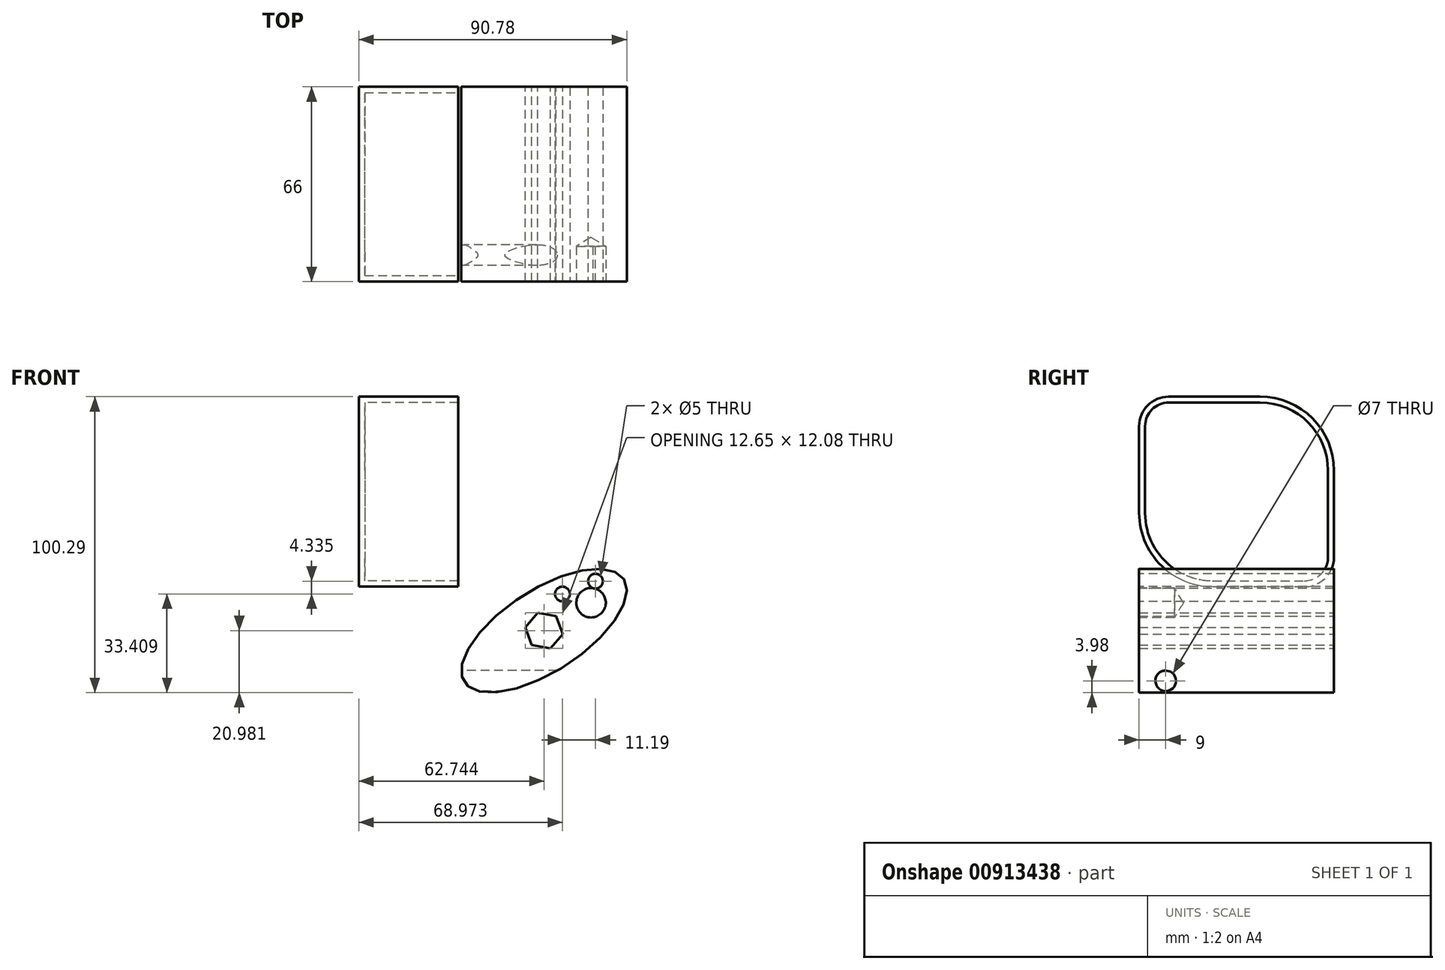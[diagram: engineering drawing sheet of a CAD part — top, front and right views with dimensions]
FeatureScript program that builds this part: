
annotation { "Feature Type Name" : "Feature", "Feature Type Description" : "" }
export const myFeature = defineFeature(function(context is Context, id is Id, definition is map)
    precondition{}
    {
        {
            var Q0;
            Q0=qCreatedBy(makeId("Front.planeOp"),FACE);
            var sketch = newSketch(context, id + "F0", { "sketchPlane" : qUnion([Q0])});
            skLineSegment(sketch, "E0.bottom", {"start": v(16.85, 32.2) * mm, "end": v(-16.85, 32.2) * mm});
            skLineSegment(sketch, "E0.top", {"start": v(16.85, -32.2) * mm, "end": v(-16.85, -32.2) * mm});
            skLineSegment(sketch, "E0.left", {"start": v(16.85, 32.2) * mm, "end": v(16.85, -32.2) * mm});
            skLineSegment(sketch, "E0.right", {"start": v(-16.85, 32.2) * mm, "end": v(-16.85, -32.2) * mm});
            skPoint(sketch, "E0.middle", {"position": v(0, 0) * mm});
            skFitSpline(sketch, "E1", {"points": [v(-72.73, 40.61) * mm, v(-61.61, 33.2) * mm, v(-67.79, 25.17) * mm, v(-64.7, 14.36) * mm, v(-62.23, -4.17) * mm, v(-71.5, -17.45) * mm, v(-62.54, -30.42) * mm], "startDerivative": vector(104.8, -43.11) * mm, "endDerivative": vector(81.86, -75.3) * mm});
            skLineSegment(sketch, "E2", {"start": v(-54.2, 48.95) * mm, "end": v(-54.2, -37.22) * mm, "construction": true});
            skFitSpline(sketch, "E3.MirrorCS", {"points": [v(-35.67, 40.61) * mm, v(-46.79, 33.2) * mm, v(-40.61, 25.17) * mm, v(-43.7, 14.36) * mm, v(-46.17, -4.17) * mm, v(-36.9, -17.45) * mm, v(-45.86, -30.42) * mm], "startDerivative": vector(-104.8, -43.11) * mm, "endDerivative": vector(-81.86, -75.3) * mm});
            skFitSpline(sketch, "E4.0", {"points": [v(-37.2, 44.31) * mm, v(-38.28, 43.86) * mm, v(-39.95, 43.18) * mm, v(-42.11, 42.23) * mm, v(-43.68, 41.48) * mm, v(-45.18, 40.7) * mm, v(-46.6, 39.84) * mm, v(-47.92, 38.87) * mm, v(-48.95, 37.88) * mm, v(-49.7, 36.9) * mm, v(-50.21, 36.02) * mm, v(-50.6, 35) * mm, v(-50.78, 34.02) * mm, v(-50.8, 33.22) * mm, v(-50.76, 32.6) * mm, v(-50.65, 32.04) * mm, v(-50.46, 31.33) * mm, v(-50.15, 30.56) * mm, v(-49.71, 29.78) * mm, v(-49.25, 29.1) * mm, v(-48.6, 28.3) * mm, v(-47.8, 27.41) * mm, v(-46.84, 26.46) * mm, v(-45.94, 25.58) * mm, v(-45.17, 24.79) * mm, v(-44.7, 24.22) * mm, v(-44.44, 23.86) * mm, v(-44.33, 23.69) * mm, v(-44.28, 23.59) * mm, v(-44.26, 23.54) * mm, v(-44.25, 23.5) * mm, v(-44.22, 23.43) * mm, v(-44.2, 23.33) * mm, v(-44.2, 23.06) * mm, v(-44.28, 22.58) * mm, v(-44.5, 21.88) * mm, v(-44.86, 21) * mm, v(-45.35, 19.96) * mm, v(-45.95, 18.8) * mm, v(-46.5, 17.71) * mm, v(-46.97, 16.79) * mm, v(-47.32, 16.06) * mm, v(-47.67, 15.3) * mm, v(-48.14, 14.29) * mm, v(-48.7, 12.96) * mm, v(-49.53, 10.76) * mm, v(-50.42, 7.87) * mm, v(-51, 4.84) * mm, v(-51.22, 2.35) * mm, v(-51.23, 0.46) * mm, v(-51.07, -1.45) * mm, v(-50.7, -3.37) * mm, v(-50.2, -4.95) * mm, v(-49.66, -6.19) * mm, v(-49.21, -7.07) * mm, v(-48.73, -7.9) * mm, v(-48.05, -8.97) * mm, v(-47.14, -10.2) * mm, v(-46.03, -11.54) * mm, v(-44.56, -13.2) * mm, v(-43.2, -14.67) * mm, v(-42.1, -15.95) * mm, v(-41.48, -16.8) * mm, v(-41.13, -17.37) * mm, v(-40.97, -17.72) * mm, v(-40.9, -17.92) * mm, v(-40.86, -18.06) * mm, v(-40.84, -18.14) * mm, v(-40.84, -18.25) * mm, v(-40.85, -18.42) * mm, v(-40.92, -18.76) * mm, v(-41.15, -19.36) * mm, v(-41.57, -20.11) * mm, v(-42.38, -21.28) * mm, v(-43.82, -22.96) * mm, v(-46.04, -25.15) * mm, v(-47.72, -26.7) * mm, v(-48.57, -27.48) * mm]});
            skEllipse(sketch, "E5", {"center": v(45.9, -47.1) * mm, "majorRadius": 32.16 * mm, "minorRadius": 13.86 * mm, "majorAxis": v(0.84, 0.54)});
            skCircle(sketch, "E6.cCircle", {"center": v(45.9, -47.1) * mm, "radius": 5.56 * mm, "construction": true});
            skLineSegment(sketch, "E6.0", {"start": v(41.76, -52.02) * mm, "end": v(39.57, -45.98) * mm});
            skLineSegment(sketch, "E6.1", {"start": v(39.57, -45.98) * mm, "end": v(43.7, -41.06) * mm});
            skLineSegment(sketch, "E6.2", {"start": v(43.7, -41.06) * mm, "end": v(50.03, -42.18) * mm});
            skLineSegment(sketch, "E6.3", {"start": v(50.03, -42.18) * mm, "end": v(52.22, -48.22) * mm});
            skLineSegment(sketch, "E6.4", {"start": v(52.22, -48.22) * mm, "end": v(48.09, -53.14) * mm});
            skLineSegment(sketch, "E6.5", {"start": v(48.09, -53.14) * mm, "end": v(41.76, -52.02) * mm});
            skPoint(sketch, "E6.0.midPoint", {"position": v(40.66, -49) * mm});
            skSolve(sketch);
        }
        {
            var Q0;
            Q0=makeQuery(id+"F0.imprint","IMPRINT",FACE,{"disambiguationData":[TD([[makeQuery(id+"F0.imprint","IMPRINT",EDGE,{"derivedFrom":sQuery(id+"F0.wireOp",EDGE,"E0.bottom")}),1.0]])]});
            var Q1;
            Q1=makeQuery(id+"F0.imprint","IMPRINT",FACE,{"disambiguationData":[TD([[makeQuery(id+"F0.imprint","IMPRINT",EDGE,{"derivedFrom":sQuery(id+"F0.wireOp",EDGE,"E5")}),1.0]])]});
            extrude(context, id + "F1", {"entities" : qUnion([Q0, Q1]), "depth" : 66 * mm, "offsetDistance" : 25 * mm});
        }
        {
            var Q0;
            Q0=makeQuery(id+"F1.opExtrude","CAP_EDGE",EDGE,{"disambiguationData":[OSD([sQuery(id+"F0.wireOp",EDGE,"E0.top")])],"isStart":false});
            var Q1;
            Q1=makeQuery(id+"F1.opExtrude","CAP_EDGE",EDGE,{"disambiguationData":[OSD([sQuery(id+"F0.wireOp",EDGE,"E0.bottom")])],"isStart":true});
            fillet(context, id + "F2", {"entities" : qUnion([Q0, Q1]), "radius" : 25 * mm, "tangentPropagation" : true, "allowEdgeOverflow" : false});
        }
        {
            var Q0;
            Q0=makeQuery(id+"F1.opExtrude","CAP_EDGE",EDGE,{"disambiguationData":[OSD([sQuery(id+"F0.wireOp",EDGE,"E0.bottom")])],"isStart":false});
            var Q1;
            Q1=makeQuery(id+"F1.opExtrude","CAP_EDGE",EDGE,{"disambiguationData":[OSD([sQuery(id+"F0.wireOp",EDGE,"E0.top")])],"isStart":true});
            fillet(context, id + "F3", {"entities" : qUnion([Q0, Q1]), "radius" : 10 * mm, "tangentPropagation" : true, "allowEdgeOverflow" : false});
        }
        {
            var Q0;
            Q0=makeQuery(id+"F1.opExtrude","SWEPT_FACE",FACE,{"disambiguationData":[OSD([sQuery(id+"F0.wireOp",EDGE,"E0.left")])]});
            shell(context, id + "F4", {"entities" : qUnion([Q0]), "thickness" : 2 * mm});
        }
        {
            var Q0;
            Q0=qCreatedBy(makeId("Right.planeOp"),FACE);
            var sketch = newSketch(context, id + "F5", { "sketchPlane" : qUnion([Q0])});
            skCircle(sketch, "E7", {"center": v(-57, -64.1) * mm, "radius": 3.5 * mm});
            skSolve(sketch);
        }
        {
            var Q0;
            Q0 = qSketchRegion(id + "F5", true);
            extrude(context, id + "F6", {"entities" : qUnion([Q0]), "operationType" : NewBodyOperationType.REMOVE, "depth" : 65.4 * mm, "offsetDistance" : 25 * mm});
        }
        {
            var Q0;
            Q0=makeQuery(id+"F1.opExtrude","CAP_FACE",FACE,{"disambiguationData":[OSD([sQuery(id+"F0.wireOp",EDGE,"E5"),sQuery(id+"F0.wireOp",EDGE,"E6.0"),sQuery(id+"F0.wireOp",EDGE,"E6.1"),sQuery(id+"F0.wireOp",EDGE,"E6.2"),sQuery(id+"F0.wireOp",EDGE,"E6.3"),sQuery(id+"F0.wireOp",EDGE,"E6.4"),sQuery(id+"F0.wireOp",EDGE,"E6.5")])],"isStart":false});
            var sketch = newSketch(context, id + "F7", { "sketchPlane" : qUnion([Q0])});
            skPoint(sketch, "E8", {"position": v(52.12, -34.67) * mm});
            skPoint(sketch, "E9", {"position": v(61.82, -37.65) * mm});
            skPoint(sketch, "E10", {"position": v(63.31, -30.34) * mm});
            skSolve(sketch);
        }
        {
            var Q0;
            Q0=sQuery(id+"F7.wireOp",VERTEX,"E8");
            var Q1;
            Q1=sQuery(id+"F7.wireOp",VERTEX,"E10");
            var Q2;
            Q2=makeQuery(id+"F1.opExtrude","SWEPT_BODY",BODY,{"disambiguationData":[OSD([sQuery(id+"F0.wireOp",EDGE,"E5"),sQuery(id+"F0.wireOp",EDGE,"E6.0"),sQuery(id+"F0.wireOp",EDGE,"E6.1"),sQuery(id+"F0.wireOp",EDGE,"E6.2"),sQuery(id+"F0.wireOp",EDGE,"E6.3"),sQuery(id+"F0.wireOp",EDGE,"E6.4"),sQuery(id+"F0.wireOp",EDGE,"E6.5")])]});
            hole(context, id + "F8", {"style" : HoleStyle.SIMPLE, "endStyle" : HoleEndStyle.THROUGH, "holeDiameter" : 5 * mm, "majorDiameter" : 5 * mm, "isTappedThrough" : true, "tappedDepth" : 12 * mm, "tapClearance" : 3, "locations" : qUnion([Q0, Q1]), "scope" : qUnion([Q2])});
        }
        {
            var Q0;
            Q0=sQuery(id+"F7.wireOp",VERTEX,"E9");
            var Q1;
            Q1=makeQuery(id+"F1.opExtrude","SWEPT_BODY",BODY,{"disambiguationData":[OSD([sQuery(id+"F0.wireOp",EDGE,"E5"),sQuery(id+"F0.wireOp",EDGE,"E6.0"),sQuery(id+"F0.wireOp",EDGE,"E6.1"),sQuery(id+"F0.wireOp",EDGE,"E6.2"),sQuery(id+"F0.wireOp",EDGE,"E6.3"),sQuery(id+"F0.wireOp",EDGE,"E6.4"),sQuery(id+"F0.wireOp",EDGE,"E6.5")])]});
            hole(context, id + "F9", {"style" : HoleStyle.SIMPLE, "endStyle" : HoleEndStyle.BLIND, "holeDiameter" : 10 * mm, "majorDiameter" : 5 * mm, "holeDepth" : 12 * mm, "isTappedThrough" : true, "tappedDepth" : 12 * mm, "tapClearance" : 3, "locations" : qUnion([Q0]), "scope" : qUnion([Q1])});
        }
    });
